AUTODESK INVENTOR PART (.ipt)
format: ipt  version: 2021.5 (Build 255421000, 421)  size: 1,189,376 bytes
history: native  units: mm
features: sketch x2
ambient origin geometry x8: Origin, YZ Plane, XZ Plane, XY Plane, X Axis, Y Axis, Z Axis, Center Point
feature tree (2):
  sketch  "Boceto2"  dims[d0=30.0mm]
  sketch  "Boceto4"  dims[d1=36.0mm d2=2.5mm d67=600.0mm d68=400.0mm d69=30.0mm d70=558.0mm d71=358.0mm d72=5.0mm d73=4.0mm d74=5.0mm d75=3.5mm d76=30.0mm d77=3.5mm d78=30.0mm d79=3.5mm d80=1.75mm d81=98.5mm d82=3.5mm d83=85.5mm d84=3.5mm d85=1.75mm d86=3.5mm d87=13.25mm d88=3.5mm d89=39.0mm d90=3.5mm d91=13.25mm d92=3.5mm d94=60.0mm d96=60.0mm d97=556.0mm d98=355.0mm d99=4.0mm d100=58.5mm d101=92.0mm d102=15.0mm d103=15.0mm d104=10.0mm d105=5.5mm]
